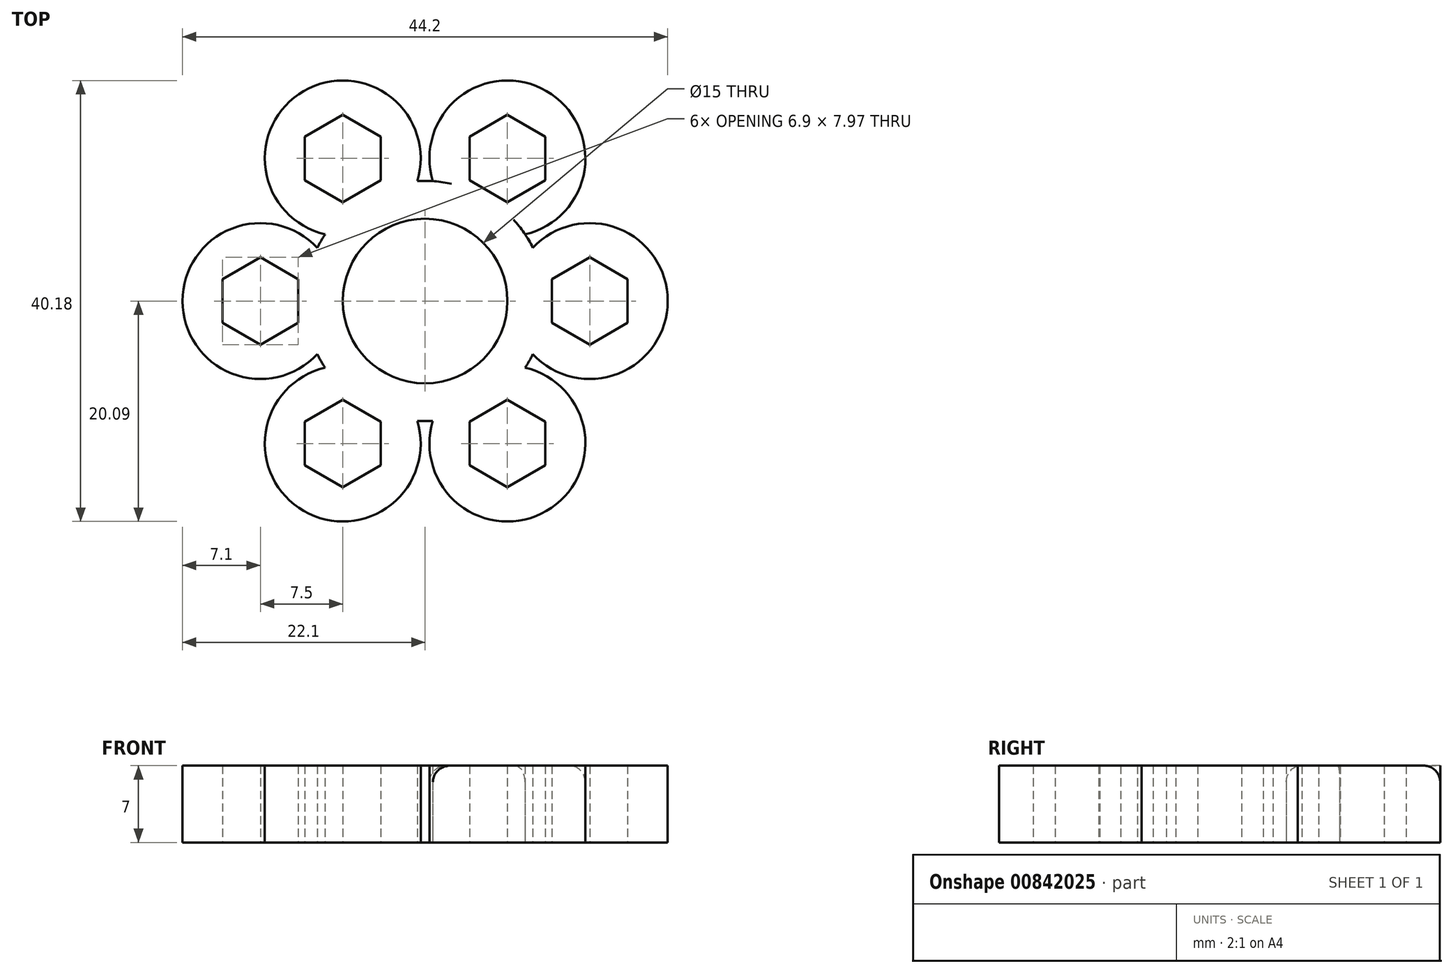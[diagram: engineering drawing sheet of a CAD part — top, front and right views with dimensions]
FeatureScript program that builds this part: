
annotation { "Feature Type Name" : "Feature", "Feature Type Description" : "" }
export const myFeature = defineFeature(function(context is Context, id is Id, definition is map)
    precondition{}
    {
        {
            var Q0;
            Q0=qCreatedBy(makeId("Top.planeOp"),FACE);
            var sketch = newSketch(context, id + "F0", { "sketchPlane" : qUnion([Q0])});
            skArc(sketch, "E0", {"start": v(-9.82, -4.85) * mm, "mid": v(-9.48, -5.48) * mm, "end": v(-9.11, -6.07) * mm});
            skCircle(sketch, "E1.cCircle", {"center": v(-15, 0) * mm, "radius": 3.45 * mm, "construction": true});
            skLineSegment(sketch, "E1.0", {"start": v(-11.55, 2) * mm, "end": v(-11.55, -2) * mm});
            skLineSegment(sketch, "E1.1", {"start": v(-11.55, -2) * mm, "end": v(-15, -3.98) * mm});
            skLineSegment(sketch, "E1.2", {"start": v(-15, -3.98) * mm, "end": v(-18.45, -2) * mm});
            skLineSegment(sketch, "E1.3", {"start": v(-18.45, -2) * mm, "end": v(-18.45, 2) * mm});
            skLineSegment(sketch, "E1.4", {"start": v(-18.45, 2) * mm, "end": v(-15, 3.98) * mm});
            skLineSegment(sketch, "E1.5", {"start": v(-15, 3.98) * mm, "end": v(-11.55, 2) * mm});
            skPoint(sketch, "E1.0.midPoint", {"position": v(-11.55, 0) * mm});
            skArc(sketch, "E2", {"start": v(-9.82, 4.85) * mm, "mid": v(-22.1, 0) * mm, "end": v(-9.82, -4.85) * mm});
            skPoint(sketch, "E3.1.0", {"position": v(-5.77, -10) * mm});
            skLineSegment(sketch, "E3.1.1", {"start": v(-7.5, -16.97) * mm, "end": v(-10.95, -14.98) * mm});
            skCircle(sketch, "E3.1.2", {"center": v(-7.5, -13) * mm, "radius": 3.45 * mm, "construction": true});
            skLineSegment(sketch, "E3.1.3", {"start": v(-10.95, -11) * mm, "end": v(-7.5, -9) * mm});
            skArc(sketch, "E3.1.4", {"start": v(-9.11, -6.07) * mm, "mid": v(-11.05, -19.14) * mm, "end": v(-0.7, -10.93) * mm});
            skLineSegment(sketch, "E3.1.5", {"start": v(-4.05, -11) * mm, "end": v(-4.05, -14.98) * mm});
            skLineSegment(sketch, "E3.1.6", {"start": v(-10.95, -14.98) * mm, "end": v(-10.95, -11) * mm});
            skLineSegment(sketch, "E3.1.7", {"start": v(-4.05, -14.98) * mm, "end": v(-7.5, -16.97) * mm});
            skLineSegment(sketch, "E3.1.8", {"start": v(-7.5, -9) * mm, "end": v(-4.05, -11) * mm});
            skPoint(sketch, "E3.2.0", {"position": v(5.77, -10) * mm});
            skLineSegment(sketch, "E3.2.1", {"start": v(10.95, -14.98) * mm, "end": v(7.5, -16.97) * mm});
            skCircle(sketch, "E3.2.2", {"center": v(7.5, -13) * mm, "radius": 3.45 * mm, "construction": true});
            skLineSegment(sketch, "E3.2.3", {"start": v(4.05, -14.98) * mm, "end": v(4.05, -11) * mm});
            skArc(sketch, "E3.2.4", {"start": v(0.7, -10.93) * mm, "mid": v(11.05, -19.14) * mm, "end": v(9.11, -6.07) * mm});
            skLineSegment(sketch, "E3.2.5", {"start": v(7.5, -9) * mm, "end": v(10.95, -11) * mm});
            skLineSegment(sketch, "E3.2.6", {"start": v(7.5, -16.97) * mm, "end": v(4.05, -14.98) * mm});
            skLineSegment(sketch, "E3.2.7", {"start": v(10.95, -11) * mm, "end": v(10.95, -14.98) * mm});
            skLineSegment(sketch, "E3.2.8", {"start": v(4.05, -11) * mm, "end": v(7.5, -9) * mm});
            skPoint(sketch, "E3.3.0", {"position": v(11.55, 0) * mm});
            skLineSegment(sketch, "E3.3.1", {"start": v(18.45, 2) * mm, "end": v(18.45, -2) * mm});
            skCircle(sketch, "E3.3.2", {"center": v(15, 0) * mm, "radius": 3.45 * mm, "construction": true});
            skLineSegment(sketch, "E3.3.3", {"start": v(15, -3.98) * mm, "end": v(11.55, -2) * mm});
            skArc(sketch, "E3.3.4", {"start": v(9.82, -4.85) * mm, "mid": v(22.1, 0) * mm, "end": v(9.82, 4.85) * mm});
            skLineSegment(sketch, "E3.3.5", {"start": v(11.55, 2) * mm, "end": v(15, 3.98) * mm});
            skLineSegment(sketch, "E3.3.6", {"start": v(18.45, -2) * mm, "end": v(15, -3.98) * mm});
            skLineSegment(sketch, "E3.3.7", {"start": v(15, 3.98) * mm, "end": v(18.45, 2) * mm});
            skLineSegment(sketch, "E3.3.8", {"start": v(11.55, -2) * mm, "end": v(11.55, 2) * mm});
            skPoint(sketch, "E3.4.0", {"position": v(5.78, 10) * mm});
            skLineSegment(sketch, "E3.4.1", {"start": v(7.5, 16.97) * mm, "end": v(10.95, 14.98) * mm});
            skCircle(sketch, "E3.4.2", {"center": v(7.5, 13) * mm, "radius": 3.45 * mm, "construction": true});
            skLineSegment(sketch, "E3.4.3", {"start": v(10.95, 11) * mm, "end": v(7.5, 9) * mm});
            skArc(sketch, "E3.4.4", {"start": v(9.11, 6.07) * mm, "mid": v(11.05, 19.14) * mm, "end": v(0.7, 10.93) * mm});
            skLineSegment(sketch, "E3.4.5", {"start": v(4.05, 11) * mm, "end": v(4.05, 14.98) * mm});
            skLineSegment(sketch, "E3.4.6", {"start": v(10.95, 14.98) * mm, "end": v(10.95, 11) * mm});
            skLineSegment(sketch, "E3.4.7", {"start": v(4.05, 14.98) * mm, "end": v(7.5, 16.97) * mm});
            skLineSegment(sketch, "E3.4.8", {"start": v(7.5, 9) * mm, "end": v(4.05, 11) * mm});
            skPoint(sketch, "E3.5.0", {"position": v(-5.77, 10) * mm});
            skLineSegment(sketch, "E3.5.1", {"start": v(-10.95, 14.98) * mm, "end": v(-7.5, 16.97) * mm});
            skCircle(sketch, "E3.5.2", {"center": v(-7.5, 13) * mm, "radius": 3.45 * mm, "construction": true});
            skLineSegment(sketch, "E3.5.3", {"start": v(-4.05, 14.98) * mm, "end": v(-4.05, 11) * mm});
            skArc(sketch, "E3.5.4", {"start": v(-0.7, 10.93) * mm, "mid": v(-11.05, 19.14) * mm, "end": v(-9.11, 6.07) * mm});
            skLineSegment(sketch, "E3.5.5", {"start": v(-7.5, 9) * mm, "end": v(-10.95, 11) * mm});
            skLineSegment(sketch, "E3.5.6", {"start": v(-7.5, 16.97) * mm, "end": v(-4.05, 14.98) * mm});
            skLineSegment(sketch, "E3.5.7", {"start": v(-10.95, 11) * mm, "end": v(-10.95, 14.98) * mm});
            skLineSegment(sketch, "E3.5.8", {"start": v(-4.05, 11) * mm, "end": v(-7.5, 9) * mm});
            skArc(sketch, "E4.trimOffspring", {"start": v(-9.11, 6.07) * mm, "mid": v(-9.48, 5.48) * mm, "end": v(-9.82, 4.85) * mm});
            skArc(sketch, "E5.trimOffspring", {"start": v(0.7, 10.93) * mm, "mid": v(0, 10.95) * mm, "end": v(-0.7, 10.93) * mm});
            skArc(sketch, "E6.trimOffspring", {"start": v(9.82, 4.85) * mm, "mid": v(9.48, 5.47) * mm, "end": v(9.11, 6.07) * mm});
            skArc(sketch, "E7.trimOffspring", {"start": v(9.11, -6.07) * mm, "mid": v(9.48, -5.47) * mm, "end": v(9.82, -4.85) * mm});
            skArc(sketch, "E8.trimOffspring", {"start": v(-0.7, -10.93) * mm, "mid": v(0, -10.95) * mm, "end": v(0.7, -10.93) * mm});
            skCircle(sketch, "E9", {"center": v(0, 0) * mm, "radius": 7.5 * mm});
            skSolve(sketch);
        }
        {
            var Q0;
            Q0=makeQuery(id+"F0.imprint","IMPRINT",FACE,{"disambiguationData":[TD([[makeQuery(id+"F0.imprint","IMPRINT",EDGE,{"derivedFrom":sQuery(id+"F0.wireOp",EDGE,"E0")}),1.0]])]});
            extrude(context, id + "F1", {"entities" : qUnion([Q0]), "depth" : 7 * mm, "offsetDistance" : 25 * mm});
        }
        {
            var Q0;
            Q0=makeQuery(id+"F1.opExtrude","CAP_EDGE",EDGE,{"disambiguationData":[OSD([sQuery(id+"F0.wireOp",EDGE,"E3.4.4")])],"isStart":false});
            fillet(context, id + "F2", {"entities" : qUnion([Q0]), "radius" : 1.5 * mm, "tangentPropagation" : true, "allowEdgeOverflow" : false});
        }
    });
